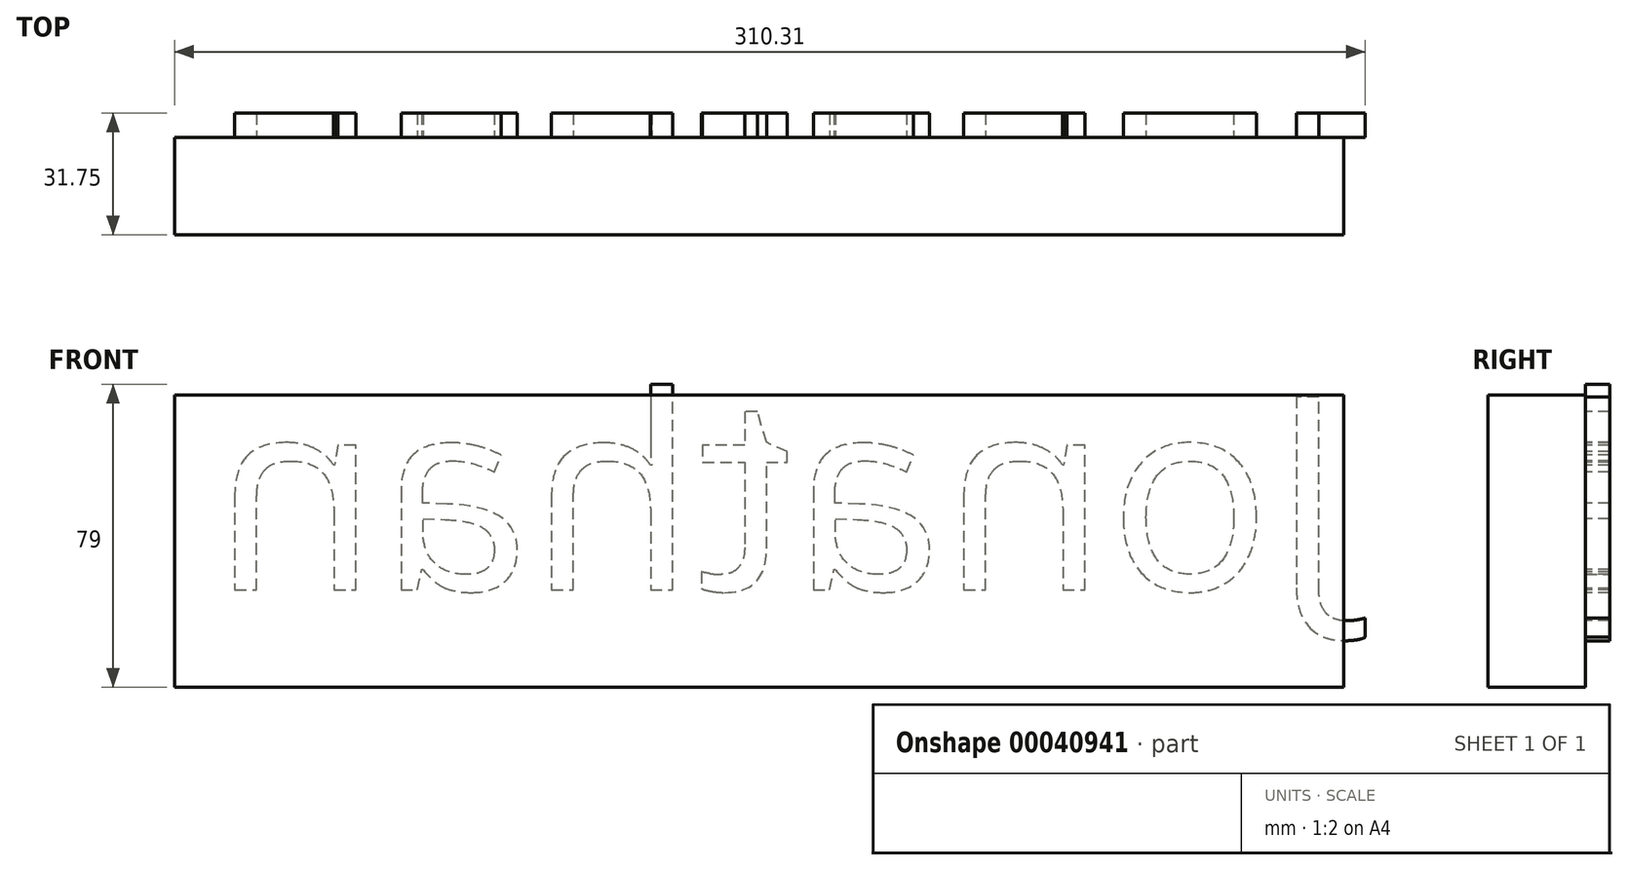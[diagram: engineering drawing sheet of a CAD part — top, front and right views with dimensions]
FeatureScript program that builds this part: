
annotation { "Feature Type Name" : "Feature", "Feature Type Description" : "" }
export const myFeature = defineFeature(function(context is Context, id is Id, definition is map)
    precondition{}
    {
        {
            var Q0;
            Q0=qCreatedBy(makeId("Front.planeOp"),FACE);
            var sketch = newSketch(context, id + "F0", { "sketchPlane" : qUnion([Q0])});
            skLineSegment(sketch, "E0.bottom", {"start": v(-76.43, 33.3) * mm, "end": v(75.97, 33.3) * mm});
            skLineSegment(sketch, "E0.top", {"start": v(-76.43, -17.5) * mm, "end": v(75.97, -17.5) * mm});
            skLineSegment(sketch, "E0.left", {"start": v(-76.43, 33.3) * mm, "end": v(-76.43, -17.5) * mm});
            skLineSegment(sketch, "E0.right", {"start": v(75.97, 33.3) * mm, "end": v(75.97, -17.5) * mm});
            skSolve(sketch);
        }
        {
            var Q0;
            Q0 = qSketchRegion(id + "F0", true);
            extrude(context, id + "F1", {"entities" : qUnion([Q0]), "depth" : 25.4 * mm});
        }
        {
            var Q0;
            Q0=makeQuery(id+"F1.opExtrude","CAP_FACE",FACE,{"disambiguationData":[OSD([sQuery(id+"F0.wireOp",EDGE,"E0.bottom"),sQuery(id+"F0.wireOp",EDGE,"E0.top"),sQuery(id+"F0.wireOp",EDGE,"E0.left"),sQuery(id+"F0.wireOp",EDGE,"E0.right")])],"isStart":true});
            var sketch = newSketch(context, id + "F2", { "sketchPlane" : qUnion([Q0])});
            skText(sketch, "E1", { "text": "Jonathan", "fontName": "OpenSans-Regular.ttf"});
            const initialGuessF2  = {"E1": [-0.07597, -0.0175, 1, 0, 0.0508]};
            skSetInitialGuess(sketch, initialGuessF2);
            skSolve(sketch);
        }
        {
            var Q0;
            Q0=makeQuery(id+"F1.opExtrude","SWEPT_FACE",FACE,{"disambiguationData":[OSD([sQuery(id+"F0.wireOp",EDGE,"E0.left")])]});
            var sketch = newSketch(context, id + "F3", { "sketchPlane" : qUnion([Q0])});
            skSolve(sketch);
        }
        {
            var Q0;
            {var subQ0=sQuery(id+"F0.wireOp",EDGE,"E0.left");Q0=makeQuery(id+"F3.imprint","IMPRINT",FACE,{"disambiguationData":[TD([[makeQuery(id+"F3.imprint","IMPRINT",EDGE,{"derivedFrom":makeQuery(id+"F1.opExtrude","CAP_EDGE",EDGE,{"disambiguationData":[OSD([subQ0])],"isStart":true})}),1.0]])]});}
            extrude(context, id + "F4", {"entities" : qUnion([Q0]), "operationType" : NewBodyOperationType.ADD, "depth" : 152.4 * mm});
        }
        {
            var Q0;
            {var subQ0=sQuery(id+"F0.wireOp",EDGE,"E0.top");Q0=makeQuery(id+"F4.boolean.opBoolean","MERGE",FACE,{"derivedFrom":[makeQuery(id+"F1.opExtrude","SWEPT_FACE",FACE,{"disambiguationData":[OSD([subQ0])]}),makeQuery(id+"F4.opExtrude","SWEPT_FACE",FACE,{"disambiguationData":[OSD([subQ0,sQuery(id+"F0.wireOp",EDGE,"E0.left")])]})]});}
            extrude(context, id + "F5", {"entities" : qUnion([Q0]), "operationType" : NewBodyOperationType.ADD, "depth" : 25.4 * mm});
        }
        {
            var Q0;
            Q0 = qSketchRegion(id + "F2", true);
            extrude(context, id + "F6", {"entities" : qUnion([Q0]), "operationType" : NewBodyOperationType.ADD, "depth" : 6.35 * mm});
        }
    });
